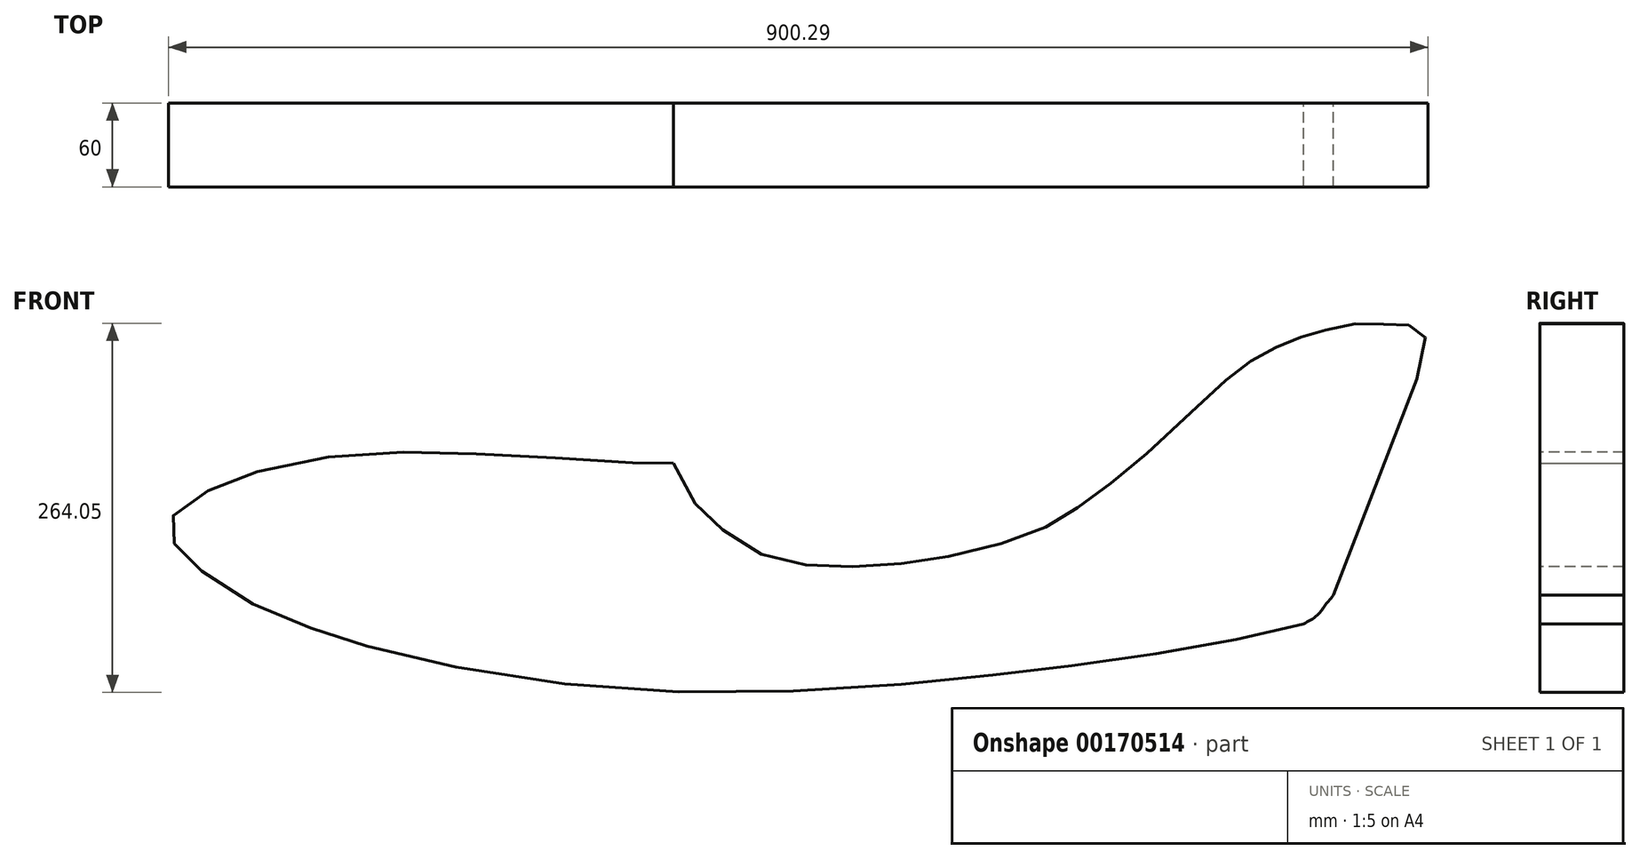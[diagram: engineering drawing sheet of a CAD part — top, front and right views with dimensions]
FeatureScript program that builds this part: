
annotation { "Feature Type Name" : "Feature", "Feature Type Description" : "" }
export const myFeature = defineFeature(function(context is Context, id is Id, definition is map)
    precondition{}
    {
        {
            var Q0;
            Q0=qCreatedBy(makeId("Front.planeOp"),FACE);
            var sketch = newSketch(context, id + "F0", { "sketchPlane" : qUnion([Q0])});
            skFitSpline(sketch, "E0", {"points": [v(-62.44, 153.7) * mm, v(-49.86, 129.06) * mm, v(-38.92, 116.39) * mm, v(-22.8, 102.56) * mm, v(0, 88.74) * mm, v(25.58, 81.83) * mm, v(50.35, 80.1) * mm, v(80.87, 80.1) * mm, v(108.52, 82.98) * mm, v(137.46, 87.75) * mm, v(173.77, 97) * mm, v(200.4, 106.68) * mm, v(215.8, 114.82) * mm, v(231.42, 125.38) * mm, v(248.58, 138.14) * mm, v(267.59, 153.46) * mm, v(297.85, 180.65) * mm, v(326.46, 207.84) * mm, v(336.82, 216.56) * mm, v(346.98, 224.45) * mm, v(356.31, 230.47) * mm, v(365.23, 235.24) * mm, v(373.94, 239.19) * mm, v(382.44, 242.51) * mm, v(390.73, 245.21) * mm, v(399.03, 247.5) * mm, v(406.7, 249.79) * mm, v(418.52, 252.28) * mm, v(428.9, 253.74) * mm, v(440.3, 253.54) * mm, v(447.35, 253.13) * mm, v(455.65, 253.34) * mm, v(463.95, 252.3) * mm, v(472.25, 249.4) * mm, v(473.1, 246.5) * mm, v(476.64, 240.61) * mm, v(469.13, 214.11) * mm], "startDerivative": vector(207.33, -709.32) * mm, "endDerivative": vector(-334.76, -854.26) * mm});
            skLineSegment(sketch, "E1", {"start": v(469.13, 214.11) * mm, "end": v(409.28, 59.35) * mm});
            skFitSpline(sketch, "E2", {"points": [v(409.28, 59.35) * mm, v(404.19, 53.3) * mm, v(401.45, 49.24) * mm, v(396.08, 43.65) * mm, v(388.17, 38.93) * mm], "startDerivative": vector(-15.54, -26) * mm, "endDerivative": vector(-29.23, -15.05) * mm});
            skFitSpline(sketch, "E3", {"points": [v(388.17, 38.93) * mm, v(323.43, 24.4) * mm, v(230.23, 10.03) * mm, v(144.13, 0) * mm, v(0, -9.97) * mm, v(-170.9, 0) * mm, v(-288.47, 24.82) * mm, v(-329.44, 38.93) * mm, v(-378.43, 61.3) * mm, v(-409.3, 85.3) * mm, v(-419.27, 96.2) * mm, v(-423.36, 104.66) * mm, v(-418.4, 118.8) * mm, v(-398.1, 132.6) * mm, v(-366.9, 145.53) * mm, v(-301.45, 159.3) * mm, v(-228.59, 161.36) * mm, v(-151.7, 157.72) * mm, v(-85.75, 153.7) * mm, v(-62.44, 153.7) * mm], "startDerivative": vector(-1074.14, -263) * mm, "endDerivative": vector(2079.32, 0) * mm});
            skSolve(sketch);
        }
        {
            var Q0;
            Q0 = qSketchRegion(id + "F0", true);
            extrude(context, id + "F1", {"entities" : qUnion([Q0]), "depth" : 60 * mm});
        }
    });
